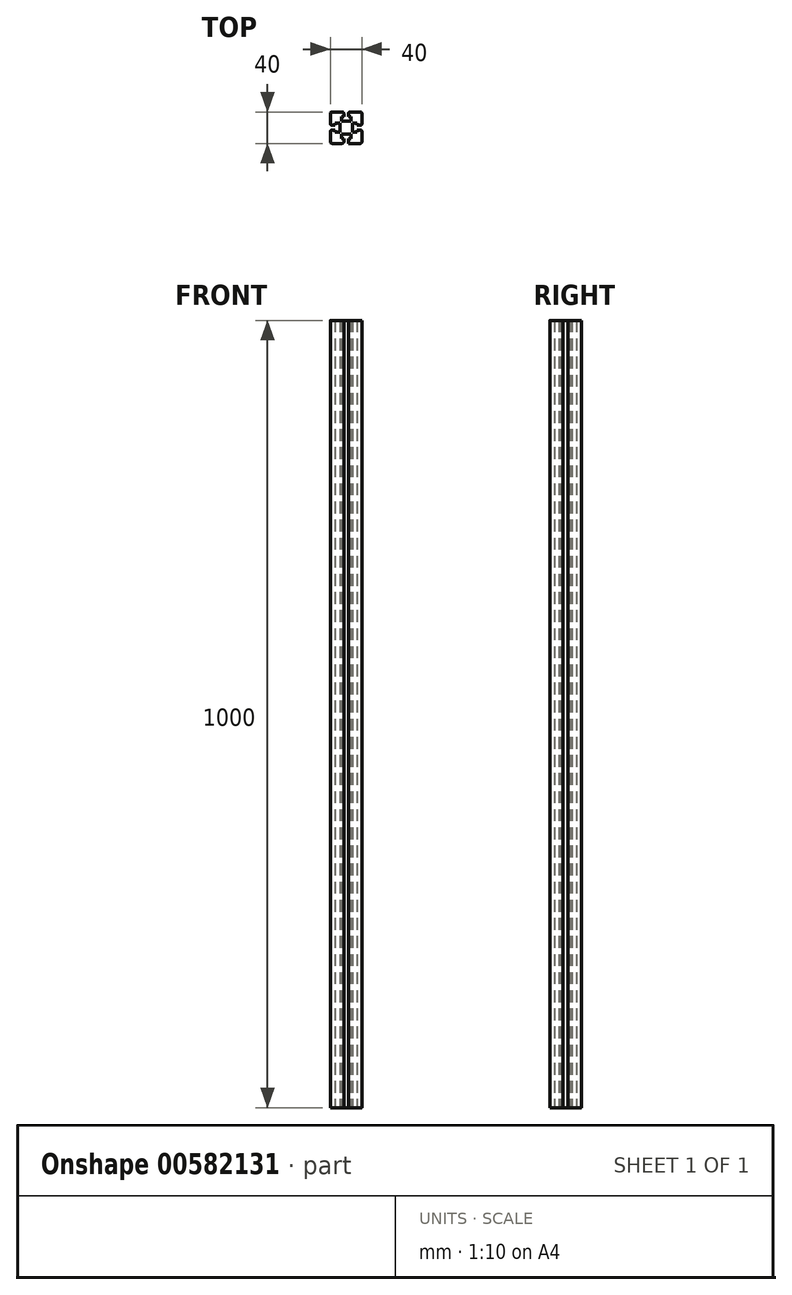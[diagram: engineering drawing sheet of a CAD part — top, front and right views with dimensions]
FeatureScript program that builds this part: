
annotation { "Feature Type Name" : "Feature", "Feature Type Description" : "" }
export const myFeature = defineFeature(function(context is Context, id is Id, definition is map)
    precondition{}
    {
        {
            var Q0;
            Q0=qCreatedBy(makeId("Top.planeOp"),FACE);
            var sketch = newSketch(context, id + "F0", { "sketchPlane" : qUnion([Q0])});
            skLineSegment(sketch, "E0.bottom", {"start": v(20, 20) * mm, "end": v(3, 20) * mm});
            skLineSegment(sketch, "E0.top", {"start": v(20, -20) * mm, "end": v(3, -20) * mm});
            skLineSegment(sketch, "E0.left", {"start": v(20, 20) * mm, "end": v(20, 3) * mm});
            skLineSegment(sketch, "E0.right", {"start": v(-20, 20) * mm, "end": v(-20, 3) * mm});
            skPoint(sketch, "E0.middle", {"position": v(0, 0) * mm});
            skLineSegment(sketch, "E1.left", {"start": v(3, 14) * mm, "end": v(3, 20) * mm});
            skLineSegment(sketch, "E1.right", {"start": v(-3, 14) * mm, "end": v(-3, 20) * mm});
            skPoint(sketch, "E1.middle", {"position": v(0, 20) * mm});
            skLineSegment(sketch, "E2.bottom", {"start": v(-6, 14) * mm, "end": v(-3, 14) * mm});
            skLineSegment(sketch, "E2.top", {"start": v(-6, 8) * mm, "end": v(6, 8) * mm});
            skLineSegment(sketch, "E2.left", {"start": v(-6, 14) * mm, "end": v(-6, 8) * mm});
            skLineSegment(sketch, "E2.right", {"start": v(6, 14) * mm, "end": v(6, 8) * mm});
            skPoint(sketch, "E2.middle", {"position": v(0, 11) * mm});
            skLineSegment(sketch, "E3.bottom", {"start": v(14, 3) * mm, "end": v(20, 3) * mm});
            skLineSegment(sketch, "E3.top", {"start": v(14, -3) * mm, "end": v(20, -3) * mm});
            skPoint(sketch, "E3.middle", {"position": v(20, 0) * mm});
            skLineSegment(sketch, "E4.bottom", {"start": v(14, 6) * mm, "end": v(8, 6) * mm});
            skLineSegment(sketch, "E4.top", {"start": v(14, -6) * mm, "end": v(8, -6) * mm});
            skLineSegment(sketch, "E4.left", {"start": v(14, 6) * mm, "end": v(14, 3) * mm});
            skLineSegment(sketch, "E4.right", {"start": v(8, 6) * mm, "end": v(8, -6) * mm});
            skPoint(sketch, "E4.middle", {"position": v(11, 0) * mm});
            skPoint(sketch, "E4.middle.positionSnap0", {"position": v(14, 0) * mm});
            skPoint(sketch, "E4.centerSnap0", {"position": v(14, 0) * mm});
            skLineSegment(sketch, "E5.left", {"start": v(3.1, -14) * mm, "end": v(3, -20) * mm});
            skLineSegment(sketch, "E5.right", {"start": v(-2.9, -14) * mm, "end": v(-3, -20) * mm});
            skPoint(sketch, "E5.middle", {"position": v(0, -20) * mm});
            skLineSegment(sketch, "E6.bottom", {"start": v(6, -14) * mm, "end": v(3.1, -14) * mm});
            skLineSegment(sketch, "E6.top", {"start": v(6, -8) * mm, "end": v(-6, -8) * mm});
            skLineSegment(sketch, "E6.left", {"start": v(6, -14) * mm, "end": v(6, -8) * mm});
            skLineSegment(sketch, "E6.right", {"start": v(-6, -14) * mm, "end": v(-6, -8) * mm});
            skPoint(sketch, "E6.middle", {"position": v(0, -11) * mm});
            skLineSegment(sketch, "E7.bottom", {"start": v(-14, -3) * mm, "end": v(-20, -3) * mm});
            skLineSegment(sketch, "E7.top", {"start": v(-14, 3) * mm, "end": v(-20, 3) * mm});
            skPoint(sketch, "E7.middle", {"position": v(-20, 0) * mm});
            skLineSegment(sketch, "E8.bottom", {"start": v(-14, 6) * mm, "end": v(-8, 6) * mm});
            skLineSegment(sketch, "E8.top", {"start": v(-14, -6) * mm, "end": v(-8, -6) * mm});
            skLineSegment(sketch, "E8.left", {"start": v(-14, 6) * mm, "end": v(-14, 3) * mm});
            skLineSegment(sketch, "E8.right", {"start": v(-8, 6) * mm, "end": v(-8, -6) * mm});
            skPoint(sketch, "E8.middle", {"position": v(-11, 0) * mm});
            skPoint(sketch, "E8.cornerSnap0", {"position": v(-14, 0) * mm});
            skPoint(sketch, "E9.orphan", {"position": v(-3, 26) * mm});
            skPoint(sketch, "E10.orphan", {"position": v(3, 26) * mm});
            skLineSegment(sketch, "E11.trimOffspring", {"start": v(-3, 20) * mm, "end": v(-20, 20) * mm});
            skLineSegment(sketch, "E12.trimOffspring", {"start": v(3, 14) * mm, "end": v(6, 14) * mm});
            skLineSegment(sketch, "E13.trimOffspring", {"start": v(14, -3) * mm, "end": v(14, -6) * mm});
            skLineSegment(sketch, "E14.trimOffspring", {"start": v(20, -3) * mm, "end": v(20, -20) * mm});
            skPoint(sketch, "E3.right.start.orphan", {"position": v(26, 3) * mm});
            skPoint(sketch, "E15.orphan", {"position": v(26, -3) * mm});
            skLineSegment(sketch, "E16.trimOffspring", {"start": v(-14, -3) * mm, "end": v(-14, -6) * mm});
            skPoint(sketch, "E7.right.end.orphan", {"position": v(-26, 3) * mm});
            skPoint(sketch, "E17.orphan", {"position": v(-26, -3) * mm});
            skLineSegment(sketch, "E18.trimOffspring", {"start": v(-20, -3) * mm, "end": v(-20, -20) * mm});
            skLineSegment(sketch, "E19.trimOffspring", {"start": v(-2.9, -14) * mm, "end": v(-6, -14) * mm});
            skLineSegment(sketch, "E20.trimOffspring", {"start": v(-3, -20) * mm, "end": v(-20, -20) * mm});
            skPoint(sketch, "E21.orphan", {"position": v(-3.1, -26) * mm});
            skPoint(sketch, "E22.orphan", {"position": v(2.9, -26) * mm});
            skSolve(sketch);
        }
        {
            var Q0;
            Q0 = qSketchRegion(id + "F0", true);
            extrude(context, id + "F1", {"entities" : qUnion([Q0]), "depth" : 1000 * mm, "offsetDistance" : 25 * mm});
        }
        {
            var Q0;
            Q0=makeQuery(id+"F1.opExtrude","SWEPT_EDGE",EDGE,{"disambiguationData":[OSD([sQuery(id+"F0.wireOp",EDGE,"E0.left"),sQuery(id+"F0.wireOp",EDGE,"E3.bottom")])]});
            var Q1;
            Q1=makeQuery(id+"F1.opExtrude","SWEPT_EDGE",EDGE,{"disambiguationData":[OSD([sQuery(id+"F0.wireOp",EDGE,"E0.bottom"),sQuery(id+"F0.wireOp",EDGE,"E0.left")])]});
            var Q2;
            Q2=makeQuery(id+"F1.opExtrude","SWEPT_EDGE",EDGE,{"disambiguationData":[OSD([sQuery(id+"F0.wireOp",EDGE,"E0.top"),sQuery(id+"F0.wireOp",EDGE,"E14.trimOffspring")])]});
            var Q3;
            Q3=makeQuery(id+"F1.opExtrude","SWEPT_EDGE",EDGE,{"disambiguationData":[OSD([sQuery(id+"F0.wireOp",EDGE,"E3.top"),sQuery(id+"F0.wireOp",EDGE,"E14.trimOffspring")])]});
            var Q4;
            Q4=makeQuery(id+"F1.opExtrude","SWEPT_EDGE",EDGE,{"disambiguationData":[OSD([sQuery(id+"F0.wireOp",EDGE,"E5.right"),sQuery(id+"F0.wireOp",EDGE,"E20.trimOffspring")])]});
            var Q5;
            Q5=makeQuery(id+"F1.opExtrude","SWEPT_EDGE",EDGE,{"disambiguationData":[OSD([sQuery(id+"F0.wireOp",EDGE,"E1.right"),sQuery(id+"F0.wireOp",EDGE,"E11.trimOffspring")])]});
            var Q6;
            Q6=makeQuery(id+"F1.opExtrude","SWEPT_EDGE",EDGE,{"disambiguationData":[OSD([sQuery(id+"F0.wireOp",EDGE,"E0.bottom"),sQuery(id+"F0.wireOp",EDGE,"E1.left")])]});
            var Q7;
            Q7=makeQuery(id+"F1.opExtrude","SWEPT_EDGE",EDGE,{"disambiguationData":[OSD([sQuery(id+"F0.wireOp",EDGE,"E0.right"),sQuery(id+"F0.wireOp",EDGE,"E11.trimOffspring")])]});
            var Q8;
            Q8=makeQuery(id+"F1.opExtrude","SWEPT_EDGE",EDGE,{"disambiguationData":[OSD([sQuery(id+"F0.wireOp",EDGE,"E7.bottom"),sQuery(id+"F0.wireOp",EDGE,"E18.trimOffspring")])]});
            var Q9;
            Q9=makeQuery(id+"F1.opExtrude","SWEPT_EDGE",EDGE,{"disambiguationData":[OSD([sQuery(id+"F0.wireOp",EDGE,"E0.right"),sQuery(id+"F0.wireOp",EDGE,"E7.top")])]});
            var Q10;
            Q10=makeQuery(id+"F1.opExtrude","SWEPT_EDGE",EDGE,{"disambiguationData":[OSD([sQuery(id+"F0.wireOp",EDGE,"E18.trimOffspring"),sQuery(id+"F0.wireOp",EDGE,"E20.trimOffspring")])]});
            fillet(context, id + "F2", {"entities" : qUnion([Q0, Q1, Q2, Q3, Q4, Q5, Q6, Q7, Q8, Q9, Q10]), "radius" : 2 * mm, "tangentPropagation" : true, "allowEdgeOverflow" : false});
        }
    });
